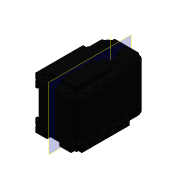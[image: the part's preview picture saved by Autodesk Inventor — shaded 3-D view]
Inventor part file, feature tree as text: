
AUTODESK INVENTOR PART (.ipt)
format: ipt  version: 2016 (Build 200138000, 138)  size: 859,648 bytes
history: native  units: mm
features: other x4, plane x1
ambient origin geometry x8: Origin, YZ Plane, XZ Plane, XY Plane, X Axis, Y Axis, Z Axis, Center Point
bodies: Body1 (feature_tree)
feature tree (5):
  other  "Bryła1"
  other  "PRT0001.ipt1"
  other  "Oś konstrukcyjna1"
  plane  "Work Plane1"
  other  "Baza1"
